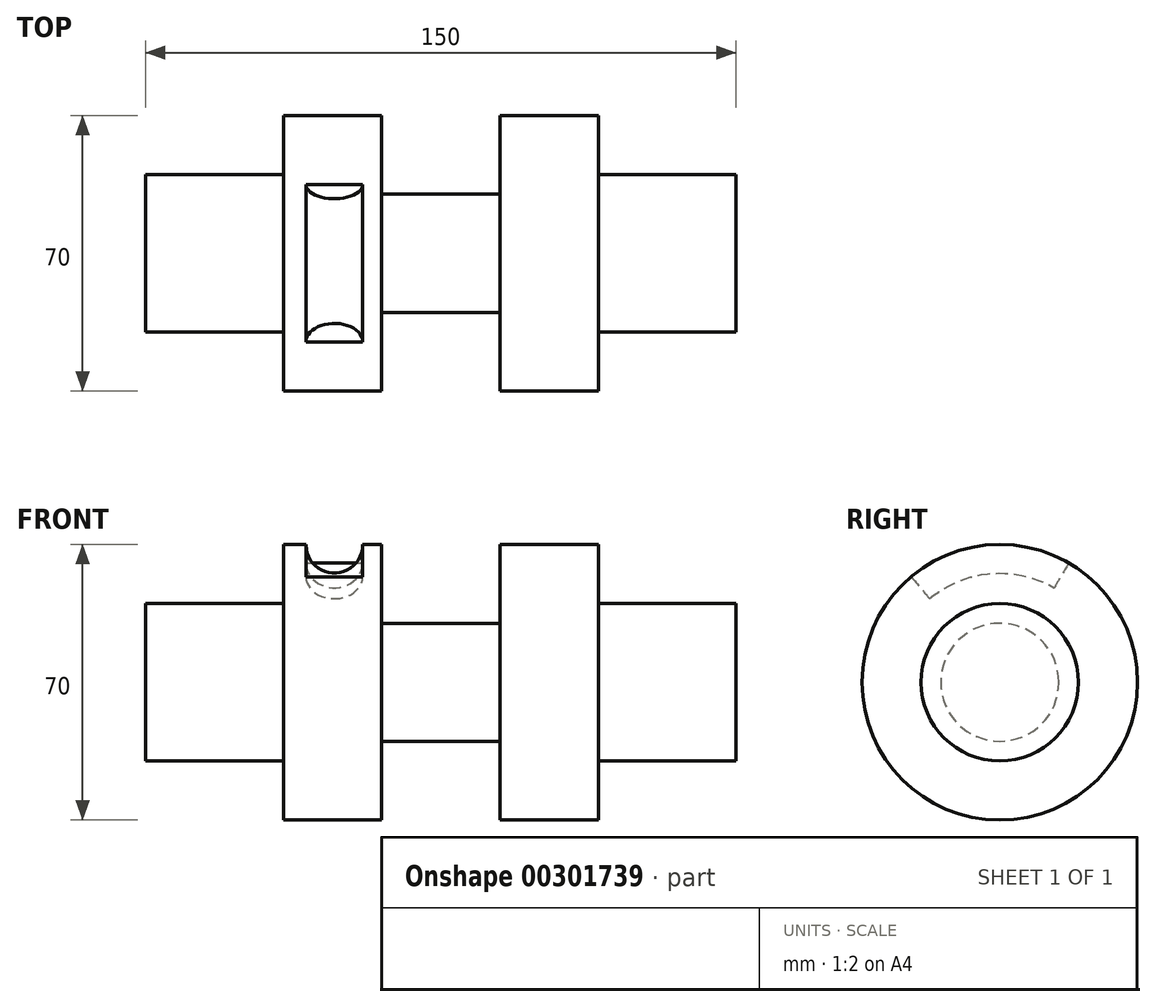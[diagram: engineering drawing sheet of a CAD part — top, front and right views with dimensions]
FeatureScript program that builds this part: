
annotation { "Feature Type Name" : "Feature", "Feature Type Description" : "" }
export const myFeature = defineFeature(function(context is Context, id is Id, definition is map)
    precondition{}
    {
        {
            var Q0;
            Q0=qCreatedBy(makeId("Front.planeOp"),FACE);
            var sketch = newSketch(context, id + "F0", { "sketchPlane" : qUnion([Q0])});
            skLineSegment(sketch, "E0", {"start": v(0, 0) * mm, "end": v(0, 20) * mm});
            skLineSegment(sketch, "E1", {"start": v(0, 20) * mm, "end": v(35, 20) * mm});
            skLineSegment(sketch, "E2", {"start": v(35, 20) * mm, "end": v(35, 35) * mm});
            skLineSegment(sketch, "E3", {"start": v(35, 35) * mm, "end": v(60, 35) * mm});
            skLineSegment(sketch, "E4", {"start": v(60, 35) * mm, "end": v(60, 15) * mm});
            skLineSegment(sketch, "E5", {"start": v(60, 15) * mm, "end": v(90, 15) * mm});
            skLineSegment(sketch, "E6", {"start": v(90, 15) * mm, "end": v(90, 35) * mm});
            skLineSegment(sketch, "E7", {"start": v(90, 35) * mm, "end": v(115, 35) * mm});
            skLineSegment(sketch, "E8", {"start": v(115, 35) * mm, "end": v(115, 20) * mm});
            skLineSegment(sketch, "E9", {"start": v(115, 20) * mm, "end": v(150, 20) * mm});
            skLineSegment(sketch, "E10", {"start": v(150, 20) * mm, "end": v(150, 0) * mm});
            skLineSegment(sketch, "E11", {"start": v(150, 0) * mm, "end": v(0, 0) * mm});
            skSolve(sketch);
        }
        {
            var Q0;
            Q0=makeQuery(id+"F0.imprint","IMPRINT",FACE,{"disambiguationData":[TD([[makeQuery(id+"F0.imprint","IMPRINT",EDGE,{"derivedFrom":sQuery(id+"F0.wireOp",EDGE,"E0")}),-1.0]])]});
            var Q1;
            Q1=sQuery(id+"F0.wireOp",EDGE,"E11");
            revolve(context, id + "F1", {"entities" : qUnion([Q0]), "axis" : qUnion([Q1]), "revolveType" : RevolveType.FULL});
        }
        {
            var Q0;
            Q0=qCreatedBy(makeId("Front.planeOp"),FACE);
            var sketch = newSketch(context, id + "F2", { "sketchPlane" : qUnion([Q0])});
            skCircle(sketch, "E12", {"center": v(47.94, 34.9) * mm, "radius": 7.19 * mm});
            skLineSegment(sketch, "E13", {"start": v(0, 0) * mm, "end": v(166.12, 0) * mm});
            skSolve(sketch);
        }
        {
            var Q0;
            Q0 = qSketchRegion(id + "F2", true);
            var Q1;
            Q1=sQuery(id+"F2.wireOp",EDGE,"E13");
            revolve(context, id + "F3", {"operationType" : NewBodyOperationType.REMOVE, "entities" : qUnion([Q0]), "axis" : qUnion([Q1]), "revolveType" : RevolveType.TWO_DIRECTIONS, "oppositeDirection" : true, "angle" : 30 * degree, "angleBack" : 320 * degree});
        }
    });
